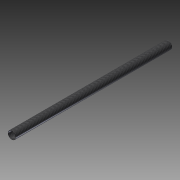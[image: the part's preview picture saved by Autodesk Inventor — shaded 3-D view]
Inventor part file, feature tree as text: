
AUTODESK INVENTOR PART (.ipt)
format: ipt  version: 2015 (Build 190159000, 159)  size: 87,552 bytes
history: native  units: in
note: dims shown in document units (in); Inventor stores cm internally (conversion verified against a paired STEP export)
features: other x3, sketch x1
ambient origin geometry x8: Origin, YZ Plane, XZ Plane, XY Plane, X Axis, Y Axis, Z Axis, Center Point
bodies: Solid1 (feature_tree)
feature tree (4):
  other  "500mm tube.ipt"
  other  "Solid1::500mm tube.ipt"
  other  "TaggingFeature1"
  sketch  "Sketch1"  dims[d0=0.3937in]
